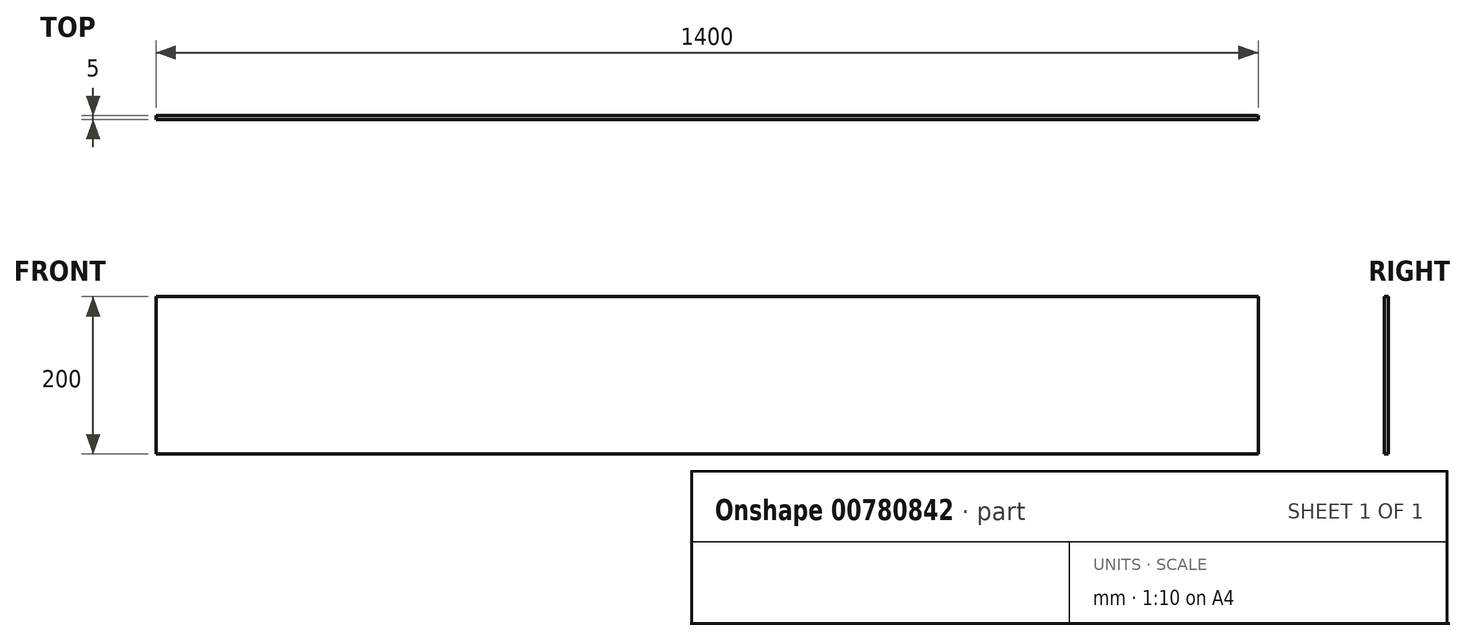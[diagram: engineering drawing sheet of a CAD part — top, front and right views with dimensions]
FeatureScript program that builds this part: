
annotation { "Feature Type Name" : "Feature", "Feature Type Description" : "" }
export const myFeature = defineFeature(function(context is Context, id is Id, definition is map)
    precondition{}
    {
        {
            var Q0;
            Q0=qCreatedBy(makeId("Front.planeOp"),FACE);
            var sketch = newSketch(context, id + "F0", { "sketchPlane" : qUnion([Q0])});
            skLineSegment(sketch, "E0.bottom", {"start": v(-700, 100) * mm, "end": v(700, 100) * mm});
            skLineSegment(sketch, "E0.top", {"start": v(-700, -100) * mm, "end": v(700, -100) * mm});
            skLineSegment(sketch, "E0.left", {"start": v(-700, 100) * mm, "end": v(-700, -100) * mm});
            skLineSegment(sketch, "E0.right", {"start": v(700, 100) * mm, "end": v(700, -100) * mm});
            skPoint(sketch, "E0.middle", {"position": v(0, 0) * mm});
            skSolve(sketch);
        }
        {
            var Q0;
            Q0=makeQuery(id+"F0.imprint","IMPRINT",FACE,{"disambiguationData":[TD([[makeQuery(id+"F0.imprint","IMPRINT",EDGE,{"derivedFrom":sQuery(id+"F0.wireOp",EDGE,"E0.bottom")}),-1.0]])]});
            extrude(context, id + "F1", {"entities" : qUnion([Q0]), "depth" : 5 * mm, "offsetDistance" : 25 * mm});
        }
    });
